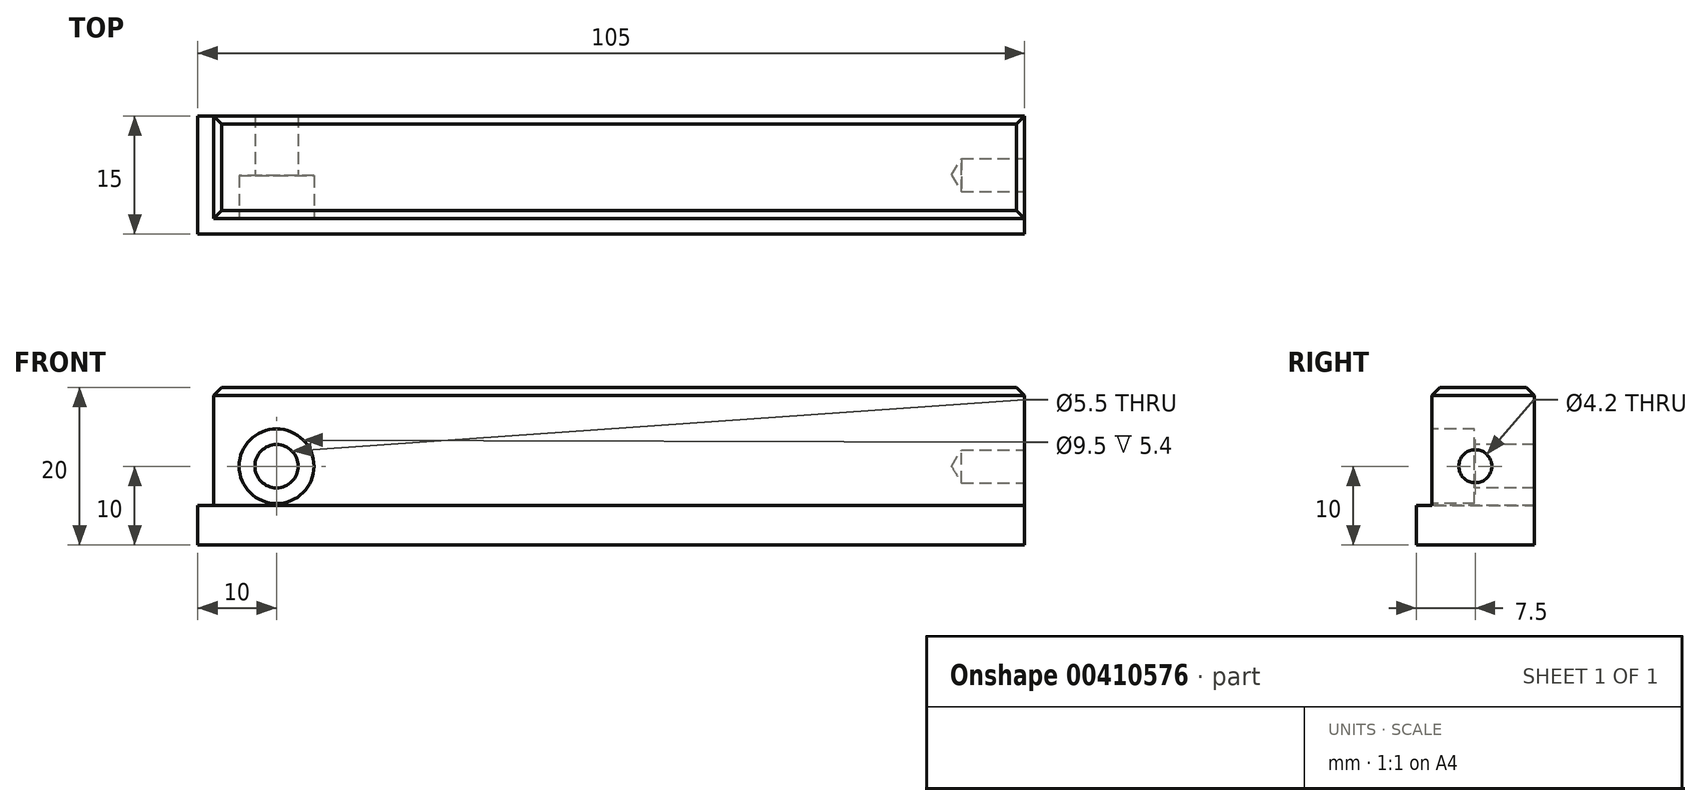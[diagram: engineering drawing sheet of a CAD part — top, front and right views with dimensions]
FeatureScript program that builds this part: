
annotation { "Feature Type Name" : "Feature", "Feature Type Description" : "" }
export const myFeature = defineFeature(function(context is Context, id is Id, definition is map)
    precondition{}
    {
        {
            var Q0;
            Q0=qCreatedBy(makeId("Top.planeOp"),FACE);
            var sketch = newSketch(context, id + "F0", { "sketchPlane" : qUnion([Q0])});
            skLineSegment(sketch, "E0.bottom", {"start": v(0, 0) * mm, "end": v(105, 0) * mm});
            skLineSegment(sketch, "E0.top", {"start": v(0, 15) * mm, "end": v(105, 15) * mm});
            skLineSegment(sketch, "E0.left", {"start": v(0, 0) * mm, "end": v(0, 15) * mm});
            skLineSegment(sketch, "E0.right", {"start": v(105, 0) * mm, "end": v(105, 15) * mm});
            skSolve(sketch);
        }
        {
            var Q0;
            Q0 = qSketchRegion(id + "F0", true);
            extrude(context, id + "F1", {"entities" : qUnion([Q0]), "depth" : 5 * mm});
        }
        {
            var Q0;
            Q0=makeQuery(id+"F1.opExtrude","CAP_FACE",FACE,{"disambiguationData":[OSD([sQuery(id+"F0.wireOp",EDGE,"E0.bottom"),sQuery(id+"F0.wireOp",EDGE,"E0.top"),sQuery(id+"F0.wireOp",EDGE,"E0.left"),sQuery(id+"F0.wireOp",EDGE,"E0.right")])],"isStart":false});
            var sketch = newSketch(context, id + "F2", { "sketchPlane" : qUnion([Q0])});
            skLineSegment(sketch, "E1.bottom", {"start": v(105, 15) * mm, "end": v(2, 15) * mm});
            skLineSegment(sketch, "E1.top", {"start": v(105, 2) * mm, "end": v(2, 2) * mm});
            skLineSegment(sketch, "E1.left", {"start": v(105, 15) * mm, "end": v(105, 2) * mm});
            skLineSegment(sketch, "E1.right", {"start": v(2, 15) * mm, "end": v(2, 2) * mm});
            skSolve(sketch);
        }
        {
            var Q0;
            Q0 = qSketchRegion(id + "F2", true);
            extrude(context, id + "F3", {"entities" : qUnion([Q0]), "operationType" : NewBodyOperationType.ADD, "depth" : 15 * mm});
        }
        {
            var Q0;
            Q0=makeQuery(id+"F3.boolean.opBoolean","MERGE",FACE,{"derivedFrom":[makeQuery(id+"F1.opExtrude","SWEPT_FACE",FACE,{"disambiguationData":[OSD([sQuery(id+"F0.wireOp",EDGE,"E0.right")])]}),makeQuery(id+"F3.opExtrude","SWEPT_FACE",FACE,{"disambiguationData":[OSD([sQuery(id+"F2.wireOp",EDGE,"E1.left")])]})]});
            var sketch = newSketch(context, id + "F4", { "sketchPlane" : qUnion([Q0])});
            skPoint(sketch, "E2", {"position": v(7.5, 10) * mm});
            skSolve(sketch);
        }
        {
            var Q0;
            Q0=sQuery(id+"F4.wireOp",VERTEX,"E2");
            var Q1;
            Q1=makeQuery(id+"F1.opExtrude","SWEPT_BODY",BODY,{"disambiguationData":[OSD([sQuery(id+"F0.wireOp",EDGE,"E0.bottom"),sQuery(id+"F0.wireOp",EDGE,"E0.top"),sQuery(id+"F0.wireOp",EDGE,"E0.left"),sQuery(id+"F0.wireOp",EDGE,"E0.right")])]});
            hole(context, id + "F5", {"style" : HoleStyle.SIMPLE, "endStyle" : HoleEndStyle.BLIND, "standardTappedOrClearance" : lookupTablePath({ "standard" : "ISO", "engagement" : "75%", "pitch" : "0.8 mm", "size" : "M5", "type" : "Tapped" }), "standardBlindInLast" : lookupTablePath({ "standard" : "ISO", "engagement" : "75%", "pitch" : "0.8 mm", "size" : "M5", "type" : "Tapped" }), "holeDiameter" : 4.2 * mm, "showTappedDepth" : true, "holeDepth" : 8 * mm, "isTappedThrough" : true, "tappedDepth" : 5.6 * mm, "tapClearance" : 3, "locations" : qUnion([Q0]), "scope" : qUnion([Q1]), "majorDiameter" : 5 * mm});
        }
        {
            var Q0;
            Q0=makeQuery(id+"F3.opExtrude","SWEPT_FACE",FACE,{"disambiguationData":[OSD([sQuery(id+"F2.wireOp",EDGE,"E1.top")])]});
            var sketch = newSketch(context, id + "F6", { "sketchPlane" : qUnion([Q0])});
            skPoint(sketch, "E3", {"position": v(10, 10) * mm});
            skSolve(sketch);
        }
        {
            var Q0;
            Q0=sQuery(id+"F6.wireOp",VERTEX,"E3");
            var Q1;
            Q1=makeQuery(id+"F1.opExtrude","SWEPT_BODY",BODY,{"disambiguationData":[OSD([sQuery(id+"F0.wireOp",EDGE,"E0.bottom"),sQuery(id+"F0.wireOp",EDGE,"E0.top"),sQuery(id+"F0.wireOp",EDGE,"E0.left"),sQuery(id+"F0.wireOp",EDGE,"E0.right")])]});
            hole(context, id + "F7", {"style" : HoleStyle.C_BORE, "endStyle" : HoleEndStyle.THROUGH, "holeDiameter" : 5.5 * mm, "cBoreDiameter" : 9.5 * mm, "cBoreDepth" : 5.4 * mm, "isTappedThrough" : true, "tappedDepth" : 5.6 * mm, "tapClearance" : 3, "locations" : qUnion([Q0]), "scope" : qUnion([Q1])});
        }
        {
            var Q0;
            Q0=makeQuery(id+"F3.opExtrude","CAP_EDGE",EDGE,{"disambiguationData":[OSD([sQuery(id+"F2.wireOp",EDGE,"E1.top")])],"isStart":false});
            var Q1;
            Q1=makeQuery(id+"F3.opExtrude","CAP_EDGE",EDGE,{"disambiguationData":[OSD([sQuery(id+"F2.wireOp",EDGE,"E1.bottom")])],"isStart":false});
            var Q2;
            Q2=makeQuery(id+"F3.opExtrude","CAP_EDGE",EDGE,{"disambiguationData":[OSD([sQuery(id+"F2.wireOp",EDGE,"E1.left")])],"isStart":false});
            var Q3;
            Q3=makeQuery(id+"F3.opExtrude","CAP_EDGE",EDGE,{"disambiguationData":[OSD([sQuery(id+"F2.wireOp",EDGE,"E1.right")])],"isStart":false});
            chamfer(context, id + "F8", {"entities" : qUnion([Q0, Q1, Q2, Q3]), "width" : 1 * mm, "tangentPropagation" : true});
        }
    });
